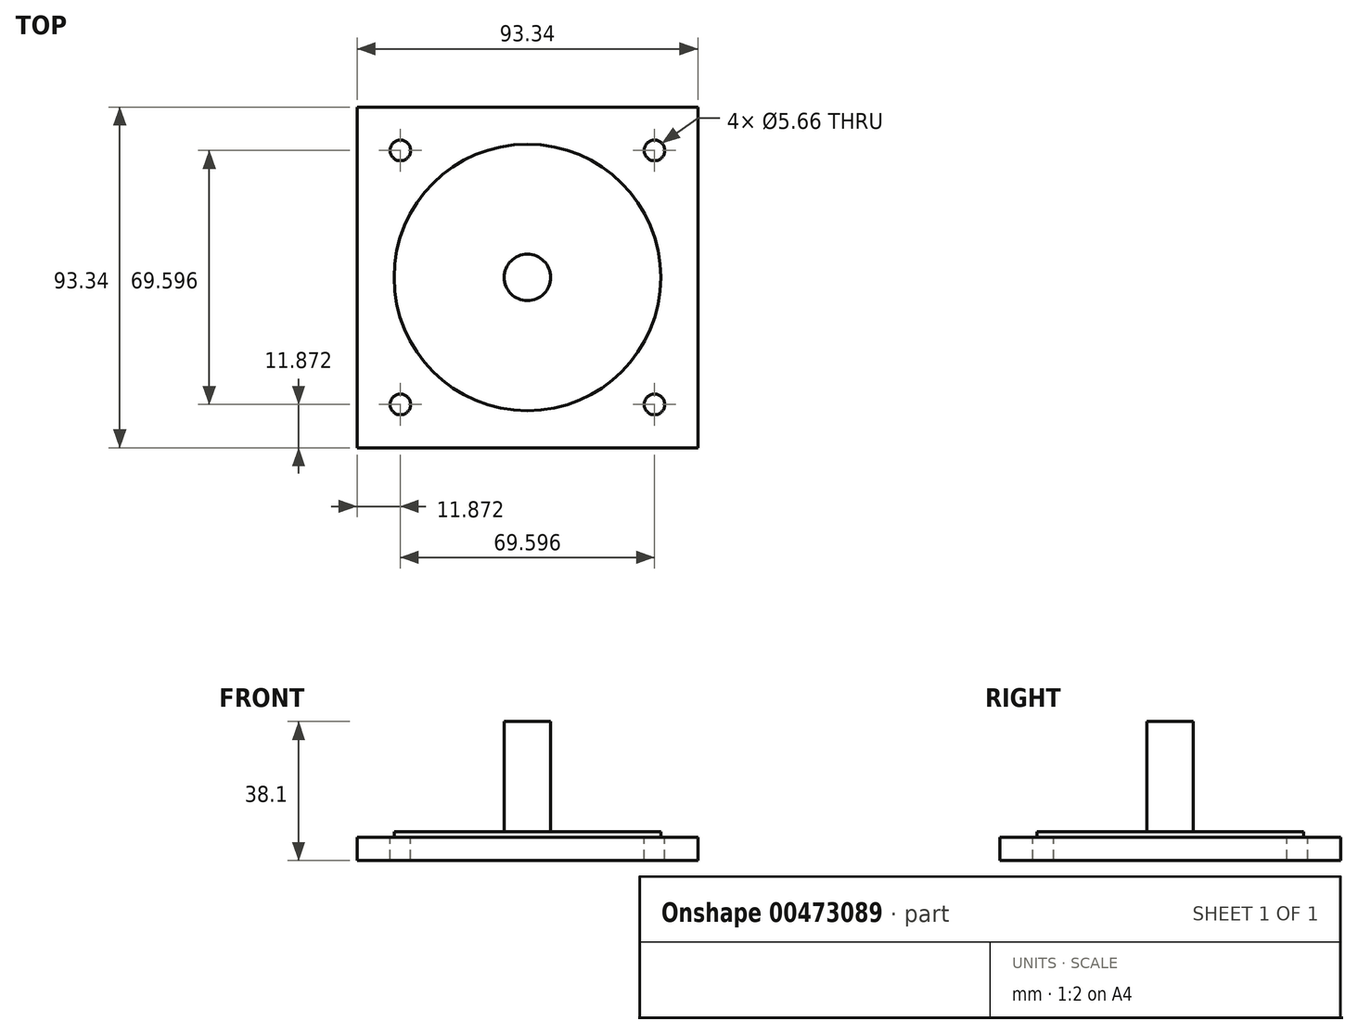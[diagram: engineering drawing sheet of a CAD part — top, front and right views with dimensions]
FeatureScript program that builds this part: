
annotation { "Feature Type Name" : "Feature", "Feature Type Description" : "" }
export const myFeature = defineFeature(function(context is Context, id is Id, definition is map)
    precondition{}
    {
        {
            var Q0;
            Q0=qCreatedBy(makeId("Top.planeOp"),FACE);
            var sketch = newSketch(context, id + "F0", { "sketchPlane" : qUnion([Q0])});
            skLineSegment(sketch, "E0.bottom", {"start": v(46.67, 46.67) * mm, "end": v(-46.67, 46.67) * mm});
            skLineSegment(sketch, "E0.top", {"start": v(46.67, -46.67) * mm, "end": v(-46.67, -46.67) * mm});
            skLineSegment(sketch, "E0.left", {"start": v(46.67, 46.67) * mm, "end": v(46.67, -46.67) * mm});
            skLineSegment(sketch, "E0.right", {"start": v(-46.67, 46.67) * mm, "end": v(-46.67, -46.67) * mm});
            skPoint(sketch, "E0.middle", {"position": v(0, 0) * mm});
            skSolve(sketch);
        }
        {
            var Q0;
            Q0 = qSketchRegion(id + "F0", true);
            extrude(context, id + "F1", {"entities" : qUnion([Q0]), "depth" : 6.35 * mm});
        }
        {
            var Q0;
            Q0=makeQuery(id+"F1.opExtrude","CAP_FACE",FACE,{"disambiguationData":[OSD([sQuery(id+"F0.wireOp",EDGE,"E0.bottom"),sQuery(id+"F0.wireOp",EDGE,"E0.top"),sQuery(id+"F0.wireOp",EDGE,"E0.left"),sQuery(id+"F0.wireOp",EDGE,"E0.right")])],"isStart":false});
            var sketch = newSketch(context, id + "F2", { "sketchPlane" : qUnion([Q0])});
            skCircle(sketch, "E1", {"center": v(0, 0) * mm, "radius": 36.51 * mm});
            skSolve(sketch);
        }
        {
            var Q0;
            Q0 = qSketchRegion(id + "F2", true);
            extrude(context, id + "F3", {"entities" : qUnion([Q0]), "operationType" : NewBodyOperationType.ADD, "depth" : 1.52 * mm});
        }
        {
            var Q0;
            Q0=makeQuery(id+"F1.opExtrude","CAP_FACE",FACE,{"disambiguationData":[OSD([sQuery(id+"F0.wireOp",EDGE,"E0.bottom"),sQuery(id+"F0.wireOp",EDGE,"E0.top"),sQuery(id+"F0.wireOp",EDGE,"E0.left"),sQuery(id+"F0.wireOp",EDGE,"E0.right")])],"isStart":false});
            var sketch = newSketch(context, id + "F4", { "sketchPlane" : qUnion([Q0])});
            skCircle(sketch, "E2", {"center": v(0, 0) * mm, "radius": 6.35 * mm});
            skSolve(sketch);
        }
        {
            var Q0;
            Q0 = qSketchRegion(id + "F4", true);
            extrude(context, id + "F5", {"entities" : qUnion([Q0]), "operationType" : NewBodyOperationType.ADD, "depth" : 31.75 * mm});
        }
        {
            var Q0;
            Q0=makeQuery(id+"F1.opExtrude","CAP_FACE",FACE,{"disambiguationData":[OSD([sQuery(id+"F0.wireOp",EDGE,"E0.bottom"),sQuery(id+"F0.wireOp",EDGE,"E0.top"),sQuery(id+"F0.wireOp",EDGE,"E0.left"),sQuery(id+"F0.wireOp",EDGE,"E0.right")])],"isStart":false});
            var sketch = newSketch(context, id + "F6", { "sketchPlane" : qUnion([Q0])});
            skLineSegment(sketch, "E3.bottom", {"start": v(34.8, 34.8) * mm, "end": v(-34.8, 34.8) * mm, "construction": true});
            skLineSegment(sketch, "E3.top", {"start": v(34.8, -34.8) * mm, "end": v(-34.8, -34.8) * mm, "construction": true});
            skLineSegment(sketch, "E3.left", {"start": v(34.8, 34.8) * mm, "end": v(34.8, -34.8) * mm, "construction": true});
            skLineSegment(sketch, "E3.right", {"start": v(-34.8, 34.8) * mm, "end": v(-34.8, -34.8) * mm, "construction": true});
            skPoint(sketch, "E3.middle", {"position": v(0, 0) * mm});
            skCircle(sketch, "E4", {"center": v(-34.8, 34.8) * mm, "radius": 2.83 * mm});
            skCircle(sketch, "E5", {"center": v(34.8, 34.8) * mm, "radius": 2.83 * mm});
            skCircle(sketch, "E6", {"center": v(34.8, -34.8) * mm, "radius": 2.83 * mm});
            skCircle(sketch, "E7", {"center": v(-34.8, -34.8) * mm, "radius": 2.83 * mm});
            skSolve(sketch);
        }
        {
            var Q0;
            Q0 = qSketchRegion(id + "F6", true);
            extrude(context, id + "F7", {"entities" : qUnion([Q0]), "operationType" : NewBodyOperationType.REMOVE, "endBound" : BoundingType.UP_TO_NEXT, "oppositeDirection" : true, "depth" : 25.4 * mm});
        }
    });
